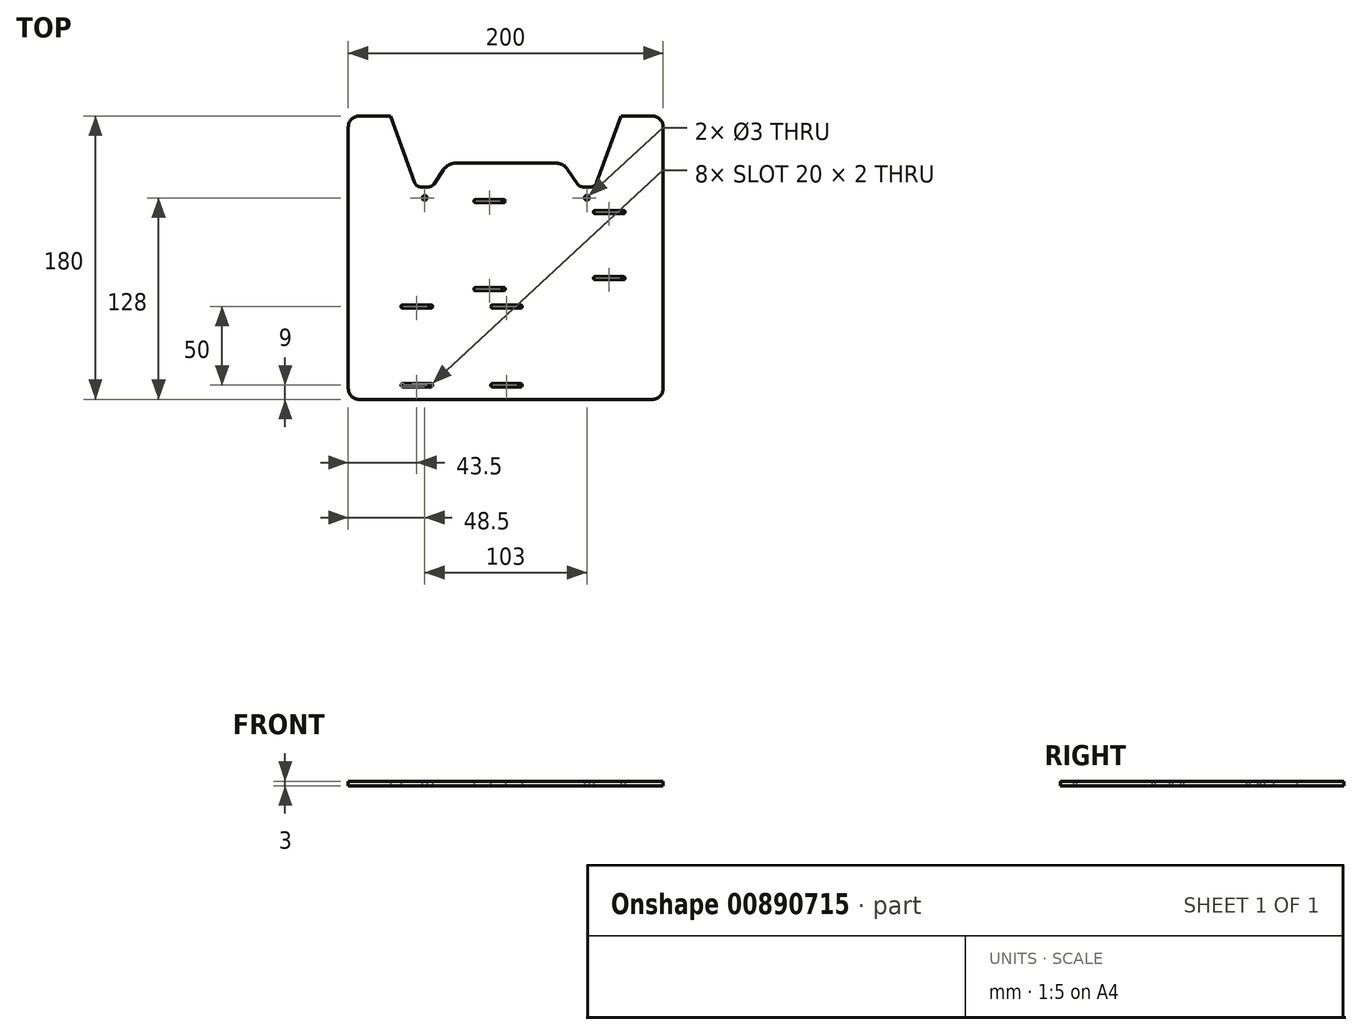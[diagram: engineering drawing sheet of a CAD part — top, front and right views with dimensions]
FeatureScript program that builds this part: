
annotation { "Feature Type Name" : "Feature", "Feature Type Description" : "" }
export const myFeature = defineFeature(function(context is Context, id is Id, definition is map)
    precondition{}
    {
        {
            var Q0;
            Q0=qCreatedBy(makeId("Top.planeOp"),FACE);
            var sketch = newSketch(context, id + "F0", { "sketchPlane" : qUnion([Q0])});
            skLineSegment(sketch, "E0", {"start": v(0, 7) * mm, "end": v(0, 173) * mm});
            skLineSegment(sketch, "E1", {"start": v(0, 253.59) * mm, "end": v(26.78, 180) * mm, "construction": true});
            skLineSegment(sketch, "E2", {"start": v(45.96, 135) * mm, "end": v(51.04, 135) * mm});
            skLineSegment(sketch, "E3", {"start": v(54.35, 136.76) * mm, "end": v(60.6, 146.03) * mm});
            skLineSegment(sketch, "E4", {"start": v(68.07, 150) * mm, "end": v(100, 150) * mm});
            skLineSegment(sketch, "E5", {"start": v(100, 0) * mm, "end": v(7, 0) * mm});
            skLineSegment(sketch, "E6", {"start": v(100, 150) * mm, "end": v(100, 0) * mm, "construction": true});
            skCircle(sketch, "E7", {"center": v(48.5, 128) * mm, "radius": 1.5 * mm});
            skLineSegment(sketch, "E8.MirrorCS", {"start": v(200, 7) * mm, "end": v(200, 173) * mm});
            skLineSegment(sketch, "E9.MirrorCS", {"start": v(200, 253.59) * mm, "end": v(173.22, 180) * mm, "construction": true});
            skLineSegment(sketch, "E10.MirrorCS", {"start": v(154.04, 135) * mm, "end": v(148.96, 135) * mm});
            skCircle(sketch, "E11.MirrorC", {"center": v(151.5, 128) * mm, "radius": 1.5 * mm});
            skLineSegment(sketch, "E12.MirrorCS", {"start": v(145.65, 136.76) * mm, "end": v(139.4, 146.03) * mm});
            skLineSegment(sketch, "E13.MirrorCS", {"start": v(131.93, 150) * mm, "end": v(100, 150) * mm});
            skLineSegment(sketch, "E14.MirrorCS", {"start": v(100, 0) * mm, "end": v(193, 0) * mm});
            skLineSegment(sketch, "E15", {"start": v(7, 180) * mm, "end": v(26.78, 180) * mm});
            skLineSegment(sketch, "E16.trimOffspring", {"start": v(173.22, 180) * mm, "end": v(193, 180) * mm});
            skLineSegment(sketch, "E17", {"start": v(0, 180) * mm, "end": v(0, 253.59) * mm, "construction": true});
            skLineSegment(sketch, "E18", {"start": v(26.78, 180) * mm, "end": v(26.78, 180) * mm});
            skLineSegment(sketch, "E19", {"start": v(26.78, 180) * mm, "end": v(42.2, 137.63) * mm});
            skLineSegment(sketch, "E20", {"start": v(200, 180) * mm, "end": v(200, 253.59) * mm, "construction": true});
            skLineSegment(sketch, "E21", {"start": v(173.22, 180) * mm, "end": v(157.8, 137.63) * mm});
            skPoint(sketch, "E22.visualSharp", {"position": v(63.28, 150) * mm});
            skArc(sketch, "E22.filletArc", {"start": v(68.07, 150) * mm, "mid": v(63.84, 148.95) * mm, "end": v(60.6, 146.03) * mm});
            skPoint(sketch, "E23.visualSharp", {"position": v(136.72, 150) * mm});
            skArc(sketch, "E23.filletArc", {"start": v(139.4, 146.03) * mm, "mid": v(136.16, 148.95) * mm, "end": v(131.93, 150) * mm});
            skPoint(sketch, "E24.visualSharp", {"position": v(43.16, 135) * mm});
            skArc(sketch, "E24.filletArc", {"start": v(42.2, 137.63) * mm, "mid": v(43.67, 135.72) * mm, "end": v(45.96, 135) * mm});
            skPoint(sketch, "E25.visualSharp", {"position": v(53.16, 135) * mm});
            skArc(sketch, "E25.filletArc", {"start": v(51.04, 135) * mm, "mid": v(52.91, 135.47) * mm, "end": v(54.35, 136.76) * mm});
            skPoint(sketch, "E26.visualSharp", {"position": v(146.84, 135) * mm});
            skArc(sketch, "E26.filletArc", {"start": v(145.65, 136.76) * mm, "mid": v(147.09, 135.47) * mm, "end": v(148.96, 135) * mm});
            skPoint(sketch, "E27.visualSharp", {"position": v(156.84, 135) * mm});
            skArc(sketch, "E27.filletArc", {"start": v(154.04, 135) * mm, "mid": v(156.33, 135.72) * mm, "end": v(157.8, 137.63) * mm});
            skPoint(sketch, "E28.visualSharp", {"position": v(0, 180) * mm});
            skArc(sketch, "E28.filletArc", {"start": v(7, 180) * mm, "mid": v(2.05, 177.95) * mm, "end": v(0, 173) * mm});
            skPoint(sketch, "E29.visualSharp", {"position": v(200, 180) * mm});
            skArc(sketch, "E29.filletArc", {"start": v(200, 173) * mm, "mid": v(197.95, 177.95) * mm, "end": v(193, 180) * mm});
            skPoint(sketch, "E30.visualSharp", {"position": v(200, 0) * mm});
            skArc(sketch, "E30.filletArc", {"start": v(193, 0) * mm, "mid": v(197.95, 2.05) * mm, "end": v(200, 7) * mm});
            skPoint(sketch, "E31.visualSharp", {"position": v(0, 0) * mm});
            skArc(sketch, "E31.filletArc", {"start": v(0, 7) * mm, "mid": v(2.05, 2.05) * mm, "end": v(7, 0) * mm});
            skLineSegment(sketch, "E32", {"start": v(79.75, 98) * mm, "end": v(175.75, 98) * mm, "construction": true});
            skLineSegment(sketch, "E33", {"start": v(156.75, 119) * mm, "end": v(174.75, 119) * mm, "construction": true});
            skLineSegment(sketch, "E34", {"start": v(80.75, 126) * mm, "end": v(98.75, 126) * mm, "construction": true});
            skArc(sketch, "E35.0.startCap", {"start": v(80.75, 125) * mm, "mid": v(79.75, 126) * mm, "end": v(80.75, 127) * mm});
            skArc(sketch, "E35.0.endCap", {"start": v(98.75, 127) * mm, "mid": v(99.75, 126) * mm, "end": v(98.75, 125) * mm});
            skLineSegment(sketch, "E35.0.left", {"start": v(80.75, 127) * mm, "end": v(98.75, 127) * mm});
            skLineSegment(sketch, "E35.0.right", {"start": v(80.75, 125) * mm, "end": v(98.75, 125) * mm});
            skArc(sketch, "E35.1.startCap", {"start": v(156.75, 118) * mm, "mid": v(155.75, 119) * mm, "end": v(156.75, 120) * mm});
            skArc(sketch, "E35.1.endCap", {"start": v(174.75, 120) * mm, "mid": v(175.75, 119) * mm, "end": v(174.75, 118) * mm});
            skLineSegment(sketch, "E35.1.left", {"start": v(156.75, 120) * mm, "end": v(174.75, 120) * mm});
            skLineSegment(sketch, "E35.1.right", {"start": v(156.75, 118) * mm, "end": v(174.75, 118) * mm});
            skPoint(sketch, "E36", {"position": v(175.75, 119) * mm});
            skLineSegment(sketch, "E37", {"start": v(34.5, 34) * mm, "end": v(109.5, 34) * mm, "construction": true});
            skLineSegment(sketch, "E38", {"start": v(34.5, 59) * mm, "end": v(52.5, 59) * mm, "construction": true});
            skLineSegment(sketch, "E39", {"start": v(91.5, 59) * mm, "end": v(109.5, 59) * mm, "construction": true});
            skLineSegment(sketch, "E40.MirrorCS", {"start": v(34.5, 9) * mm, "end": v(52.5, 9) * mm, "construction": true});
            skLineSegment(sketch, "E41.MirrorCS", {"start": v(91.5, 9) * mm, "end": v(109.5, 9) * mm, "construction": true});
            skArc(sketch, "E42.0.startCap", {"start": v(34.5, 58) * mm, "mid": v(33.5, 59) * mm, "end": v(34.5, 60) * mm});
            skArc(sketch, "E42.0.endCap", {"start": v(52.5, 60) * mm, "mid": v(53.5, 59) * mm, "end": v(52.5, 58) * mm});
            skLineSegment(sketch, "E42.0.left", {"start": v(34.5, 60) * mm, "end": v(52.5, 60) * mm});
            skLineSegment(sketch, "E42.0.right", {"start": v(34.5, 58) * mm, "end": v(52.5, 58) * mm});
            skArc(sketch, "E42.1.startCap", {"start": v(91.5, 58) * mm, "mid": v(90.5, 59) * mm, "end": v(91.5, 60) * mm});
            skArc(sketch, "E42.1.endCap", {"start": v(109.5, 60) * mm, "mid": v(110.5, 59) * mm, "end": v(109.5, 58) * mm});
            skLineSegment(sketch, "E42.1.left", {"start": v(91.5, 60) * mm, "end": v(109.5, 60) * mm});
            skLineSegment(sketch, "E42.1.right", {"start": v(91.5, 58) * mm, "end": v(109.5, 58) * mm});
            skArc(sketch, "E42.2.startCap", {"start": v(34.5, 8) * mm, "mid": v(33.5, 9) * mm, "end": v(34.5, 10) * mm});
            skArc(sketch, "E42.2.endCap", {"start": v(52.5, 10) * mm, "mid": v(53.5, 9) * mm, "end": v(52.5, 8) * mm});
            skLineSegment(sketch, "E42.2.left", {"start": v(34.5, 10) * mm, "end": v(52.5, 10) * mm});
            skLineSegment(sketch, "E42.2.right", {"start": v(34.5, 8) * mm, "end": v(52.5, 8) * mm});
            skArc(sketch, "E42.3.startCap", {"start": v(91.5, 8) * mm, "mid": v(90.5, 9) * mm, "end": v(91.5, 10) * mm});
            skArc(sketch, "E42.3.endCap", {"start": v(109.5, 10) * mm, "mid": v(110.5, 9) * mm, "end": v(109.5, 8) * mm});
            skLineSegment(sketch, "E42.3.left", {"start": v(91.5, 10) * mm, "end": v(109.5, 10) * mm});
            skLineSegment(sketch, "E42.3.right", {"start": v(91.5, 8) * mm, "end": v(109.5, 8) * mm});
            skPoint(sketch, "E43", {"position": v(151.5, 135) * mm});
            skPoint(sketch, "E44", {"position": v(48.5, 135) * mm});
            skLineSegment(sketch, "E45.MirrorCS", {"start": v(156.75, 76) * mm, "end": v(174.75, 76) * mm});
            skLineSegment(sketch, "E46.MirrorCS", {"start": v(156.75, 78) * mm, "end": v(174.75, 78) * mm});
            skArc(sketch, "E47.MirrorCS", {"start": v(174.75, 76) * mm, "mid": v(175.75, 77) * mm, "end": v(174.75, 78) * mm});
            skArc(sketch, "E48.MirrorCS", {"start": v(156.75, 78) * mm, "mid": v(155.75, 77) * mm, "end": v(156.75, 76) * mm});
            skLineSegment(sketch, "E49.MirrorCS", {"start": v(80.75, 69) * mm, "end": v(98.75, 69) * mm});
            skArc(sketch, "E50.MirrorCS", {"start": v(98.75, 69) * mm, "mid": v(99.75, 70) * mm, "end": v(98.75, 71) * mm});
            skLineSegment(sketch, "E51.MirrorCS", {"start": v(80.75, 71) * mm, "end": v(98.75, 71) * mm});
            skArc(sketch, "E52.MirrorCS", {"start": v(80.75, 71) * mm, "mid": v(79.75, 70) * mm, "end": v(80.75, 69) * mm});
            skPoint(sketch, "E53", {"position": v(79.75, 126) * mm});
            skPoint(sketch, "E54.startSnap0", {"position": v(33.5, 59) * mm});
            skPoint(sketch, "E54.endSnap0", {"position": v(53.5, 59) * mm});
            skLineSegment(sketch, "E55", {"start": v(43.5, 60) * mm, "end": v(43.5, 58) * mm, "construction": true});
            skSolve(sketch);
        }
        {
            var Q0;
            Q0=makeQuery(id+"F0.imprint","IMPRINT",FACE,{"disambiguationData":[TD([[makeQuery(id+"F0.imprint","IMPRINT",EDGE,{"derivedFrom":sQuery(id+"F0.wireOp",EDGE,"E0")}),-1.0]])]});
            extrude(context, id + "F1", {"entities" : qUnion([Q0]), "depth" : 3 * mm, "offsetDistance" : 25 * mm});
        }
    });
